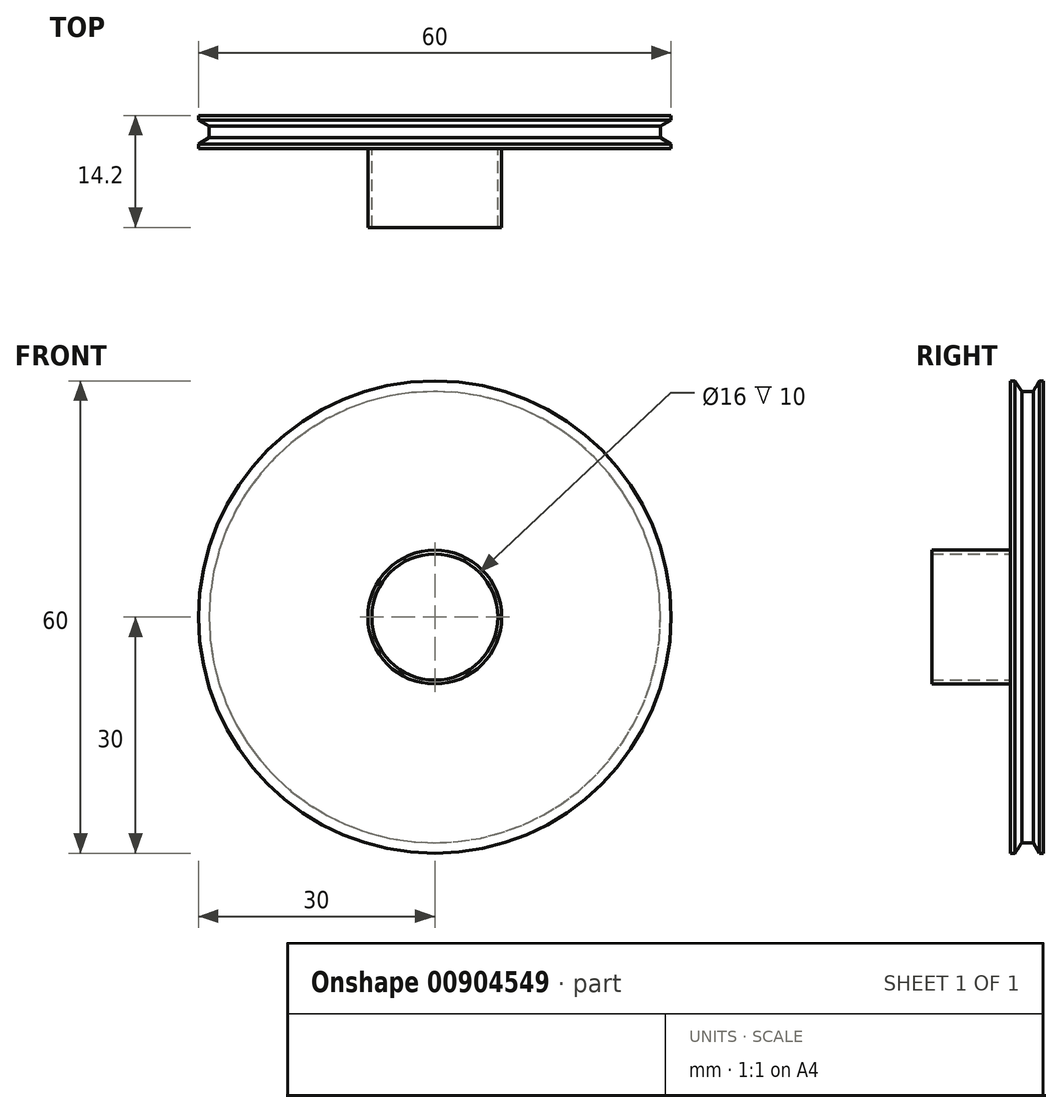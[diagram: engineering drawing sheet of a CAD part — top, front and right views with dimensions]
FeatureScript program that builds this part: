
annotation { "Feature Type Name" : "Feature", "Feature Type Description" : "" }
export const myFeature = defineFeature(function(context is Context, id is Id, definition is map)
    precondition{}
    {
        {
            var Q0;
            Q0=qCreatedBy(makeId("Front.planeOp"),FACE);
            var sketch = newSketch(context, id + "F0", { "sketchPlane" : qUnion([Q0])});
            skCircle(sketch, "E0", {"center": v(0, 0) * mm, "radius": 30 * mm});
            skSolve(sketch);
        }
        {
            var Q0;
            Q0=qSketchRegion(id+"F0",true);
            extrude(context, id + "F1", {"entities" : qUnion([Q0]), "depth" : 4.2 * mm, "offsetDistance" : 25 * mm});
        }
        {
            var Q0;
            Q0=makeQuery(id+"F1.opExtrude","CAP_FACE",FACE,{"disambiguationData":[OSD([sQuery(id+"F0.wireOp",EDGE,"E0")])],"isStart":false});
            var sketch = newSketch(context, id + "F2", { "sketchPlane" : qUnion([Q0])});
            skCircle(sketch, "E1", {"center": v(0, 0) * mm, "radius": 8.5 * mm});
            skCircle(sketch, "E2", {"center": v(0, 0) * mm, "radius": 8 * mm});
            skSolve(sketch);
        }
        {
            var Q0;
            Q0=makeQuery(id+"F2.imprint","IMPRINT",FACE,{"disambiguationData":[TD([[makeQuery(id+"F2.imprint","IMPRINT",EDGE,{"derivedFrom":sQuery(id+"F2.wireOp",EDGE,"E1")}),1.0]])]});
            extrude(context, id + "F3", {"entities" : qUnion([Q0]), "operationType" : NewBodyOperationType.ADD, "depth" : 10 * mm, "offsetDistance" : 25 * mm});
        }
        {
            var Q0;
            Q0=qCreatedBy(makeId("Top.planeOp"),FACE);
            var sketch = newSketch(context, id + "F4", { "sketchPlane" : qUnion([Q0])});
            skLineSegment(sketch, "E3", {"start": v(30.56, -4) * mm, "end": v(28.67, -2.79) * mm});
            skLineSegment(sketch, "E4", {"start": v(28.67, -2.79) * mm, "end": v(28.67, -1.31) * mm});
            skLineSegment(sketch, "E5", {"start": v(28.67, -1.31) * mm, "end": v(30.56, -0.21) * mm});
            skLineSegment(sketch, "E6", {"start": v(30.56, -0.21) * mm, "end": v(30.56, -4) * mm});
            skLineSegment(sketch, "E7", {"start": v(0, 0) * mm, "end": v(0, -5.27) * mm});
            skSolve(sketch);
        }
        {
            var Q0;
            Q0=makeQuery(id+"F4.imprint","IMPRINT",FACE,{"disambiguationData":[TD([[makeQuery(id+"F4.imprint","IMPRINT",EDGE,{"derivedFrom":sQuery(id+"F4.wireOp",EDGE,"E3")}),-1.0]])]});
            var Q1;
            Q1=sQuery(id+"F4.wireOp",EDGE,"E7");
            revolve(context, id + "F5", {"operationType" : NewBodyOperationType.REMOVE, "surfaceOperationType" : NewSurfaceOperationType.NEW, "entities" : qUnion([Q0]), "axis" : qUnion([Q1]), "revolveType" : RevolveType.FULL, "oppositeDirection" : true});
        }
    });
